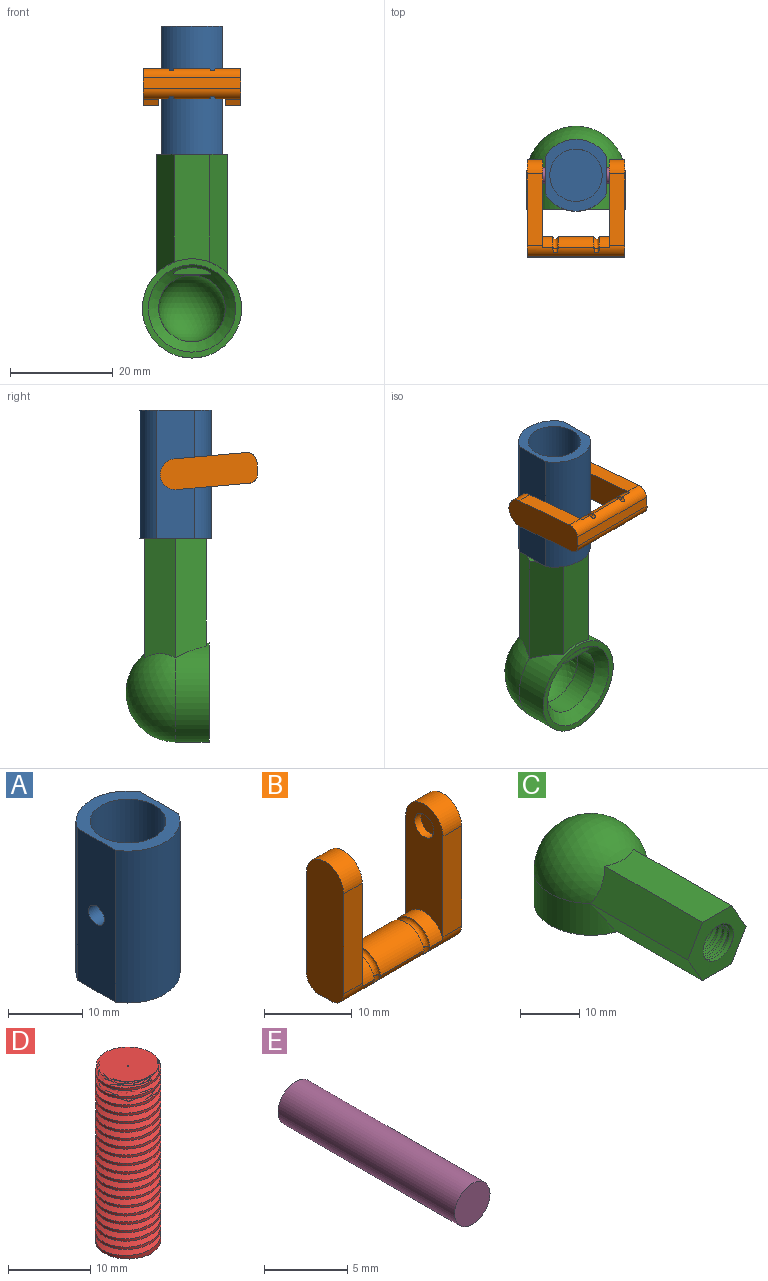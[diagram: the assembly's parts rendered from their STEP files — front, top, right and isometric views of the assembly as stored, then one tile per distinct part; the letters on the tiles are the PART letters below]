
ASSEMBLY  parts=5 mates=4
PART A: 11 faces, bbox 12x14x25 mm
  f0: plane 25x7.21mm, normal (1,0,0), area 173.2mm2, adj f1,f3,f4,f5,f10
  f1: cylinder r=7mm len=25mm, axis (0,0,-1), area 360.4mm2, adj f0,f2,f4,f5
  f2: plane 25x7.21mm, normal (-1,0,0), area 173.2mm2, adj f1,f3,f4,f5,f10
  f3: cylinder r=7mm len=25mm, axis (0,0,-1), area 360.4mm2, adj f0,f2,f4,f5
  f4: plane 14x12mm, normal (0,0,1), area 62.5mm2, adj f0,f1,f2,f3,f6
  f5: plane 14x12mm, normal (0,0,-1), area 92mm2, adj f0,f1,f2,f3,f8
  f6: cylinder r=5.1mm len=10.2mm, axis (0,0,1), area 320.4mm2, adj f4,f7
  f7: plane 10.2x10.2mm, normal (0,0,1), area 81.7mm2, adj f6
  f8: cylinder r=4.07mm len=10mm, axis (0,0,-1), area 256mm2, adj f5,f9
  f9: plane 8.15x8.15mm, normal (0,0,-1), area 52.2mm2, adj f8
  f10: cylinder r=1.5mm len=12mm, axis (-1,0,0), area 113.1mm2, adj f0,f2
PART B: 26 faces, bbox 19x7.8x19 mm
  f0: cylinder r=2mm len=19mm, axis (1,0,0), area 52.1mm2, adj f1,f2,f4,f5,f6,f7,f8,f9
  f1: cylinder r=3mm len=5.9mm, axis (1,0,0), area 16.6mm2, adj f0,f6,f12,f15
  f2: cylinder r=3mm len=7mm, axis (1,0,0), area 58.2mm2, adj f0,f12,f14,f15
  f3: plane 14x3mm, normal (0,-1,0), area 42mm2, adj f6,f7,f12,f24
  f4: plane 14x3mm, normal (0,1,0), area 42mm2, adj f0,f6,f7,f24
  f5: plane 17.45x6mm, normal (-1,0,0), area 82.4mm2, adj f0,f10,f11,f12,f13,f22,f25
  f6: plane 17.45x6mm, normal (1,0,0), area 82.4mm2, adj f0,f1,f3,f4,f12,f21,f24
  f7: plane 19x6mm, normal (-1,0,0), area 108.4mm2, adj f0,f3,f4,f8,f12,f24
  f8: plane 19x2mm, normal (0,0,-1), area 38mm2, adj f0,f7,f9,f12
  f9: plane 19x6mm, normal (1,0,0), area 108.4mm2, adj f0,f8,f10,f11,f12,f25
  f10: plane 14x3mm, normal (0,-1,0), area 42mm2, adj f5,f9,f12,f25
  f11: plane 14x3mm, normal (0,1,0), area 42mm2, adj f0,f5,f9,f25
  f12: cylinder r=2mm len=19mm, axis (-1,0,0), area 52mm2, adj f1,f2,f3,f5,f6,f7,f8,f9
  f13: cylinder r=3mm len=5.9mm, axis (1,0,0), area 16.6mm2, adj f0,f5,f12,f14
  f14: bspline ~7.83x6.3mm, area 11.6mm2, adj f2,f13,f17,f18
  f15: bspline ~7.83x6.3mm, area 11.6mm2, adj f1,f2,f16,f19
  f16: cylinder r=0.5mm len=1mm, axis (0,0,1), area 1.1mm2, adj f12,f15
  f17: cylinder r=0.5mm len=1mm, axis (0,0,1), area 1.1mm2, adj f12,f14
  f18: extruded ~1x0.89mm, area 0.8mm2, adj f0,f14
  f19: extruded ~1x0.89mm, area 0.8mm2, adj f0,f15
  f20: plane 3.1x3.1mm, normal (1,0,0), area 7.5mm2, adj f21
  f21: cylinder r=1.55mm len=3.1mm, axis (-1,0,0), area 9.7mm2, adj f6,f20
  f22: cylinder r=1.55mm len=3.1mm, axis (-1,0,0), area 9.7mm2, adj f5,f23
  f23: plane 3.1x3.1mm, normal (-1,0,0), area 7.5mm2, adj f22
  f24: cylinder r=3mm len=6mm, axis (1,0,0), area 28.3mm2, adj f3,f4,f6,f7
  f25: cylinder r=3mm len=6mm, axis (1,0,0), area 28.3mm2, adj f5,f9,f10,f11
PART C: 34 faces, bbox 21.8x42.7x18.7 mm
  f0: cylinder r=9.65mm len=19.3mm, axis (0,0,1), area 329.5mm2, adj f1,f5,f10,f11,f12
  f1: sphere r=9.65mm, area 502.1mm2, adj f0,f13,f14,f15
  f2: cone r=8.5mm half-angle=45deg, axis (0,0,-1), area 123.5mm2, adj f4,f5,f6,f7,f8,f9
  f3: sphere r=6.5mm, area 265.5mm2, adj f4
  f4: cylinder r=6.5mm len=13mm, axis (0,0,1), area 185.8mm2, adj f2,f3
  f5: plane 19.3x19.3mm, normal (0,0,-1), area 65.6mm2, adj f0,f2
  f6: plane 7.31x1.25mm, normal (0,1,0), area 6.7mm2, adj f2,f7,f8,f9
  f7: plane 0.46x0.33mm, normal (-0.87,0,-0.5), area 0.1mm2, adj f2,f6,f8
  f8: plane 6.93x1.25mm, normal (0,0,-1), area 6.9mm2, adj f2,f6,f7,f9
  f9: plane 0.46x0.33mm, normal (0.87,0,-0.5), area 0.1mm2, adj f2,f6,f8
  f10: plane 23.71x6.43mm, normal (0.87,0,-0.5), area 152.1mm2, adj f0,f11,f13,f16
  f11: plane 20.99x6.93mm, normal (0,0,-1), area 142.5mm2, adj f0,f10,f12,f16
  f12: plane 23.71x6.43mm, normal (-0.87,0,-0.5), area 152.1mm2, adj f0,f11,f14,f16
  f13: plane 25.79x8.5mm, normal (0.87,0,0.5), area 157.4mm2, adj f1,f10,f15,f16
  f14: plane 23.28x6mm, normal (-0.87,0,0.5), area 157.4mm2, adj f1,f12,f15,f16
  f15: plane 25.79x9.43mm, normal (0,0,1), area 157.4mm2, adj f1,f13,f14,f16
  f16: plane 14.19x12.33mm, normal (0,-1,0), area 85.3mm2, adj f10,f11,f12,f13,f14,f15,f28,f32
  f17: cylinder r=3.32mm len=6.65mm, axis (0,-1,0), area 9.8mm2, adj f18,f29,f32,f33
  f18: cylinder r=3.32mm len=6.65mm, axis (0,-1,0), area 9.8mm2, adj f17,f19,f32,f33
  f19: cylinder r=3.32mm len=6.65mm, axis (0,-1,0), area 9.8mm2, adj f18,f20,f32,f33
  f20: cylinder r=3.32mm len=6.65mm, axis (0,-1,0), area 9.8mm2, adj f19,f21,f32,f33
  f21: cylinder r=3.32mm len=6.65mm, axis (0,-1,0), area 9.8mm2, adj f20,f22,f32,f33
  f22: cylinder r=3.32mm len=6.65mm, axis (0,-1,0), area 9.8mm2, adj f21,f23,f32,f33
  f23: cylinder r=3.32mm len=6.65mm, axis (0,-1,0), area 9.8mm2, adj f22,f24,f32,f33
  f24: cylinder r=3.32mm len=6.65mm, axis (0,-1,0), area 9.8mm2, adj f23,f25,f32,f33
  f25: cylinder r=3.32mm len=6.65mm, axis (0,-1,0), area 9.8mm2, adj f24,f26,f32,f33
  f26: cylinder r=3.32mm len=6.65mm, axis (0,-1,0), area 9.8mm2, adj f25,f27,f32,f33
  f27: cylinder r=3.32mm len=6.65mm, axis (0,-1,0), area 9.8mm2, adj f26,f28,f32,f33
  f28: cylinder r=3.32mm len=6.65mm, axis (0,-1,0), area 7.9mm2, adj f16,f27,f32,f33
  f29: cylinder r=3.32mm len=6.65mm, axis (0,-1,0), area 18mm2, adj f17,f30,f31,f33
  f30: plane 6.65x6.65mm, normal (0,-1,0), area 34.7mm2, adj f29
  f31: plane 0.78x0.64mm, normal (0.95,0,-0.31), area 0.3mm2, adj f29,f32,f33
  f32: bspline ~15.76x8mm, area 218.1mm2, adj f16,f17,f18,f19,f20,f21,f22,f23
  f33: bspline ~16.29x8.15mm, area 223.4mm2, adj f16,f17,f18,f19,f20,f21,f22,f23
PART D: 7 faces, bbox 8.4x9.7x26.9 mm
  f0: cylinder r=4mm len=26mm, axis (0,0,-1), area -19.2mm2, adj f1,f2,f4,f5,f6
  f1: plane 7.99x7.91mm, normal (0,0,1), area 43.8mm2, adj f0,f3,f4,f6
  f2: plane 8x8mm, normal (0,0,-1), area 50.3mm2, adj f0,f3,f4
  f3: cylinder r=0.05mm len=26mm, axis (0,0,-1), area 8.2mm2, adj f1,f2
  f4: bspline ~26.49x9.24mm, area 415.8mm2, adj f0,f1,f2,f5,f6
  f5: plane 0.89x0.74mm, normal (-0.95,0.31,0), area 0.3mm2, adj f0,f4,f6
  f6: bspline ~26.07x9.24mm, area 406.9mm2, adj f0,f1,f4,f5
PART E: 3 faces, bbox 3x15x3 mm
  f0: cylinder r=1.5mm len=15mm, axis (0,1,0), area 141.4mm2, adj f1,f2
  f1: plane 3x3mm, normal (0,-1,0), area 7.1mm2, adj f0
  f2: plane 3x3mm, normal (0,1,0), area 7.1mm2, adj f0
PLACE A t=(0,0,-14)mm
PLACE B rot(axis=(-1,0,0),95deg) t=(6.5,-12.22,-3.44)mm
PLACE C rot(axis=(-1,0,0),90deg) t=(0,0,15.13)mm
PLACE D t=(48.34,0,-30)mm
PLACE E rot(axis=(0,0,1),90deg) t=(-7.5,31.74,-5.91)mm
MATE fastened E.f0 <-> A.f10  axis (-1,0,0) through (0,0,-1.5)mm
MATE fastened D.f0 <-> A.f1  axis (0,0,1) through (0,0,-4)mm
MATE fastened D.f0 <-> C.f17  axis (0,0,-1) through (0,0,-30)mm
MATE revolute B.f24 <-> E.f0  axis (-1,0,0) through (-7.5,0,-1.5)mm
